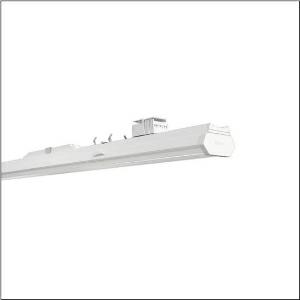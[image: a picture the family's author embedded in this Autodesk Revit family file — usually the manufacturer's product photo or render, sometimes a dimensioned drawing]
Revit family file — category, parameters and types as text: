
# Revit family: licross_r__11_protected_mo_51td117n485g_c933
name_source: partatom
category: Lighting Fixtures
units: mm (PartAtom-declared; Revit-internal decimal feet)

## family parameters
Cut with Voids When Loaded = No
Host = Face
Light Source = No
Part Type = Normal
Room Calculation Point = No
Round Connector Dimension = Use Diameter
Shared = No

## types (1)
- Licross® 11 Protected MO (1 x LED, 8680 lm, 48.6 W, 4000K)
    Apparent Load = 49 VA
    CIE Flux Codes = 83 94 98 100 100
    Color Rendering = 80
    Color Temperature = 4000K
    Default Elevation = 1800 mm
    Description = Licross® 11 Protected MO, luminaire insert, of sheet steel, galvanised, coil coated, white, length: 1.500mm, width: 90mm, height: 101mm, LED rated luminous flux: 8.680lm, light colour: 840, control gear: ON/OFF, control gear: ECG, with plug, 3-pole, with phase selection, mains connection: 220..240V, AC, 50/60Hz, halogen-free wiring, primary light control with lens, of plastic, primary optical cover: cover, of PMMA, light emission: direct with ceiling illumination distribution, primary light characteristic: symmetric, protection rating (complete): IP54, insulation class (complete): insulation class I (protective earthing), certification: CE, ENEC, VDE, UKCA, protection symbol: D if used in an environment with non-conductive dust loads with corresponding accessories, impact resistance: IK06, corresponds to IFS (International Featured Standards) requirements for safety and quality in the food industry, reducing of maximum allowable ambient temperature of 5°C with ceiling mounting, LABS conformity tested according to VDMA 24364:2018-05, packaging unit: 1 piece
    Height = 92 mm
    Lamp = 1 x LED
    Lamp Light Flux = 8680 lm
    Lamp Power = 48.6 W
    Lamp count = 1
    Length = 1500 mm
    Luminous efficacy = 179 lm/W
    Manufacturer = Siteco
    ModVariant = No
    Model = 51TD117N485G
    Mounting Place = Ceiling
    Mounting Type = Pendant
    Number of Poles = 1
    OnlyDefault = Yes
    Power Factor = 1
    Product Name = Licross® 11 Protected MO
    Product group = luminaire insert
    ProductGroupID = 902
    Protection Class = Protection class I
    Protection Degree = IP 54
    RLX_Detail_Level = 1
    RlxData = <blob elided: 20341 chars, md5=dfb33ccc>
    Socket = socket
    Standby Power = 0 W
    System Light Flux = 8680 lm
    System Power = 49 W
    Type Comments = Product without accessories
    Type Image = l_1256145.jpg
    URL = http://relux.com
    VarID = ---
    Voltage = 0 V
    Weight = 0.00 kg
    Width = 88 mm

## geometry (parser evidence)
native form markers: Blend x4, Sweep x12
no freeform markers — native parametric forms only
